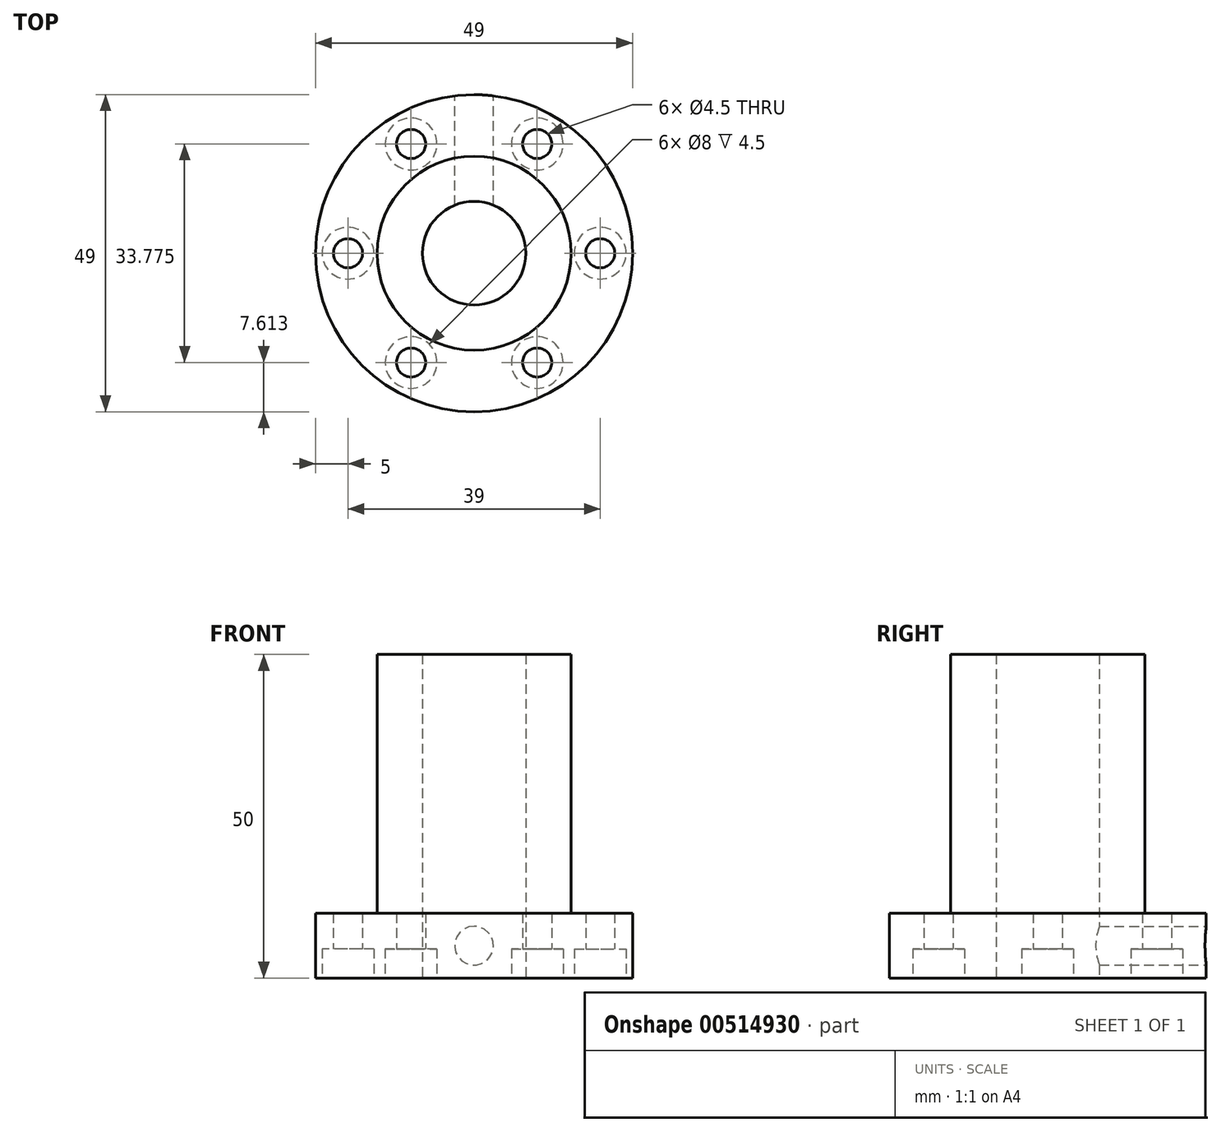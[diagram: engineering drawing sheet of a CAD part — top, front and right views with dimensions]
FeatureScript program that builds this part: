
annotation { "Feature Type Name" : "Feature", "Feature Type Description" : "" }
export const myFeature = defineFeature(function(context is Context, id is Id, definition is map)
    precondition{}
    {
        {
            var Q0;
            Q0=qCreatedBy(makeId("Front.planeOp"),FACE);
            var sketch = newSketch(context, id + "F0", { "sketchPlane" : qUnion([Q0])});
            skLineSegment(sketch, "E0", {"start": v(8, 0) * mm, "end": v(8, 50) * mm});
            skLineSegment(sketch, "E1", {"start": v(8, 50) * mm, "end": v(15, 50) * mm});
            skLineSegment(sketch, "E2", {"start": v(15, 50) * mm, "end": v(15, 10) * mm});
            skLineSegment(sketch, "E3", {"start": v(15, 10) * mm, "end": v(24.5, 10) * mm});
            skLineSegment(sketch, "E4", {"start": v(24.5, 10) * mm, "end": v(24.5, 0) * mm});
            skLineSegment(sketch, "E5", {"start": v(24.5, 0) * mm, "end": v(8, 0) * mm});
            skLineSegment(sketch, "E6", {"start": v(0, 112.5) * mm, "end": v(0, -29.18) * mm});
            skSolve(sketch);
        }
        {
            var Q0;
            Q0=makeQuery(id+"F0.imprint","IMPRINT",FACE,{"disambiguationData":[TD([[makeQuery(id+"F0.imprint","IMPRINT",EDGE,{"derivedFrom":sQuery(id+"F0.wireOp",EDGE,"E0")}),-1.0]])]});
            var Q1;
            Q1=sQuery(id+"F0.wireOp",EDGE,"E6");
            revolve(context, id + "F1", {"entities" : qUnion([Q0]), "axis" : qUnion([Q1]), "revolveType" : RevolveType.SYMMETRIC, "oppositeDirection" : true, "angle" : 60 * degree});
        }
        {
            var Q0;
            Q0=makeQuery(id+"F1.opRevolve","SWEPT_FACE",FACE,{"disambiguationData":[OSD([sQuery(id+"F0.wireOp",EDGE,"E5")])]});
            var sketch = newSketch(context, id + "F2", { "sketchPlane" : qUnion([Q0])});
            skPoint(sketch, "E7", {"position": v(19.5, 0) * mm});
            skSolve(sketch);
        }
        {
            var Q0;
            Q0=sQuery(id+"F2.wireOp",VERTEX,"E7");
            var Q1;
            Q1=makeQuery(id+"F1.opRevolve","SWEPT_BODY",BODY,{"disambiguationData":[OSD([sQuery(id+"F0.wireOp",EDGE,"E0"),sQuery(id+"F0.wireOp",EDGE,"E1"),sQuery(id+"F0.wireOp",EDGE,"E2"),sQuery(id+"F0.wireOp",EDGE,"E3"),sQuery(id+"F0.wireOp",EDGE,"E4"),sQuery(id+"F0.wireOp",EDGE,"E5")])]});
            hole(context, id + "F3", {"style" : HoleStyle.C_BORE, "endStyle" : HoleEndStyle.THROUGH, "holeDiameter" : 4.5 * mm, "cBoreDiameter" : 8 * mm, "cBoreDepth" : 4.5 * mm, "isTappedThrough" : true, "tappedDepth" : 12 * mm, "tapClearance" : 3, "locations" : qUnion([Q0]), "scope" : qUnion([Q1])});
        }
        {
            var Q0;
            Q0=makeQuery(id+"F1.opRevolve","SWEPT_BODY",BODY,{"disambiguationData":[OSD([sQuery(id+"F0.wireOp",EDGE,"E0"),sQuery(id+"F0.wireOp",EDGE,"E1"),sQuery(id+"F0.wireOp",EDGE,"E2"),sQuery(id+"F0.wireOp",EDGE,"E3"),sQuery(id+"F0.wireOp",EDGE,"E4"),sQuery(id+"F0.wireOp",EDGE,"E5")])]});
            var Q1;
            Q1=sQuery(id+"F0.wireOp",EDGE,"E6");
            circularPattern(context, id + "F4", {"entities" : qUnion([Q0]), "axis" : qUnion([Q1]), "angle" : 360 * degree, "instanceCount" : 6, "equalSpace" : true});
        }
        {
            var Q0;
            Q0=makeQuery(id+"F4.opPattern","COPY",BODY,{"derivedFrom":makeQuery(id+"F1.opRevolve","SWEPT_BODY",BODY,{"disambiguationData":[OSD([sQuery(id+"F0.wireOp",EDGE,"E0"),sQuery(id+"F0.wireOp",EDGE,"E1"),sQuery(id+"F0.wireOp",EDGE,"E2"),sQuery(id+"F0.wireOp",EDGE,"E3"),sQuery(id+"F0.wireOp",EDGE,"E4"),sQuery(id+"F0.wireOp",EDGE,"E5")])]}),"instanceName":"1"});
            var Q1;
            Q1=makeQuery(id+"F1.opRevolve","SWEPT_BODY",BODY,{"disambiguationData":[OSD([sQuery(id+"F0.wireOp",EDGE,"E0"),sQuery(id+"F0.wireOp",EDGE,"E1"),sQuery(id+"F0.wireOp",EDGE,"E2"),sQuery(id+"F0.wireOp",EDGE,"E3"),sQuery(id+"F0.wireOp",EDGE,"E4"),sQuery(id+"F0.wireOp",EDGE,"E5")])]});
            var Q2;
            Q2=makeQuery(id+"F4.opPattern","COPY",BODY,{"derivedFrom":makeQuery(id+"F1.opRevolve","SWEPT_BODY",BODY,{"disambiguationData":[OSD([sQuery(id+"F0.wireOp",EDGE,"E0"),sQuery(id+"F0.wireOp",EDGE,"E1"),sQuery(id+"F0.wireOp",EDGE,"E2"),sQuery(id+"F0.wireOp",EDGE,"E3"),sQuery(id+"F0.wireOp",EDGE,"E4"),sQuery(id+"F0.wireOp",EDGE,"E5")])]}),"instanceName":"5"});
            var Q3;
            Q3=makeQuery(id+"F4.opPattern","COPY",BODY,{"derivedFrom":makeQuery(id+"F1.opRevolve","SWEPT_BODY",BODY,{"disambiguationData":[OSD([sQuery(id+"F0.wireOp",EDGE,"E0"),sQuery(id+"F0.wireOp",EDGE,"E1"),sQuery(id+"F0.wireOp",EDGE,"E2"),sQuery(id+"F0.wireOp",EDGE,"E3"),sQuery(id+"F0.wireOp",EDGE,"E4"),sQuery(id+"F0.wireOp",EDGE,"E5")])]}),"instanceName":"4"});
            var Q4;
            Q4=makeQuery(id+"F4.opPattern","COPY",BODY,{"derivedFrom":makeQuery(id+"F1.opRevolve","SWEPT_BODY",BODY,{"disambiguationData":[OSD([sQuery(id+"F0.wireOp",EDGE,"E0"),sQuery(id+"F0.wireOp",EDGE,"E1"),sQuery(id+"F0.wireOp",EDGE,"E2"),sQuery(id+"F0.wireOp",EDGE,"E3"),sQuery(id+"F0.wireOp",EDGE,"E4"),sQuery(id+"F0.wireOp",EDGE,"E5")])]}),"instanceName":"3"});
            var Q5;
            Q5=makeQuery(id+"F4.opPattern","COPY",BODY,{"derivedFrom":makeQuery(id+"F1.opRevolve","SWEPT_BODY",BODY,{"disambiguationData":[OSD([sQuery(id+"F0.wireOp",EDGE,"E0"),sQuery(id+"F0.wireOp",EDGE,"E1"),sQuery(id+"F0.wireOp",EDGE,"E2"),sQuery(id+"F0.wireOp",EDGE,"E3"),sQuery(id+"F0.wireOp",EDGE,"E4"),sQuery(id+"F0.wireOp",EDGE,"E5")])]}),"instanceName":"2"});
            booleanBodies(context, id + "F5", {"operationType" : BooleanOperationType.UNION, "tools" : qUnion([Q0, Q1, Q2, Q3, Q4, Q5])});
        }
        {
            var Q0;
            Q0=qCreatedBy(makeId("Right.planeOp"),FACE);
            var sketch = newSketch(context, id + "F6", { "sketchPlane" : qUnion([Q0])});
            skLineSegment(sketch, "E8", {"start": v(24.5, 10) * mm, "end": v(24.5, 0) * mm});
            skPoint(sketch, "E9", {"position": v(24.5, 5) * mm});
            skSolve(sketch);
        }
        {
            var Q0;
            Q0=qCreatedBy(makeId("Front.planeOp"),FACE);
            var Q1;
            Q1=sQuery(id+"F6.wireOp",VERTEX,"E9");
            cPlane(context, id + "F7", {"entities" : qUnion([Q0, Q1]), "cplaneType" : CPlaneType.PLANE_POINT, "offset" : 32 * mm, "oppositeDirection" : true, "width" : 150 * mm, "height" : 150 * mm});
        }
        {
            var Q0;
            Q0=qCreatedBy(id+"F7.planeOp",FACE);
            var sketch = newSketch(context, id + "F8", { "sketchPlane" : qUnion([Q0])});
            skCircle(sketch, "E10", {"center": v(0, 5) * mm, "radius": 3 * mm});
            skSolve(sketch);
        }
        {
            var Q0;
            Q0=makeQuery(id+"F8.imprint","IMPRINT",FACE,{"disambiguationData":[TD([[makeQuery(id+"F8.imprint","IMPRINT",EDGE,{"derivedFrom":sQuery(id+"F8.wireOp",EDGE,"E10")}),1.0]])]});
            extrude(context, id + "F9", {"entities" : qUnion([Q0]), "operationType" : NewBodyOperationType.REMOVE, "depth" : 25 * mm, "offsetDistance" : 25 * mm});
        }
    });
